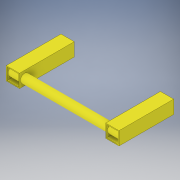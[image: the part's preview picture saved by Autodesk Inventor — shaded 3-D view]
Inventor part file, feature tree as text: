
AUTODESK INVENTOR PART (.ipt)
format: ipt  version: 2017 SP1 (Build 210196100, 196)  size: 131,072 bytes
history: native  units: in
note: dims shown in document units (in); Inventor stores cm internally (conversion verified against a paired STEP export)
features: extrude x2, sketch x2
ambient origin geometry x8: Origin, YZ Plane, XZ Plane, XY Plane, X Axis, Y Axis, Z Axis, Center Point
bodies: Solid1 (feature_tree)
feature tree (4):
  extrude  "Extrusion1"  Depth=2.0in
  extrude  "Extrusion2"  Depth=0.125in
  sketch  "Sketch1"  dims[d0=13.0in d1=2.0in]
  sketch  "Sketch2"  dims[d2=0.125in d3=0.125in d4=8.25in d5=0.0in d6=1.25in d7=0.75in d8=0.125in d9=8.25in d10=0.0in]
